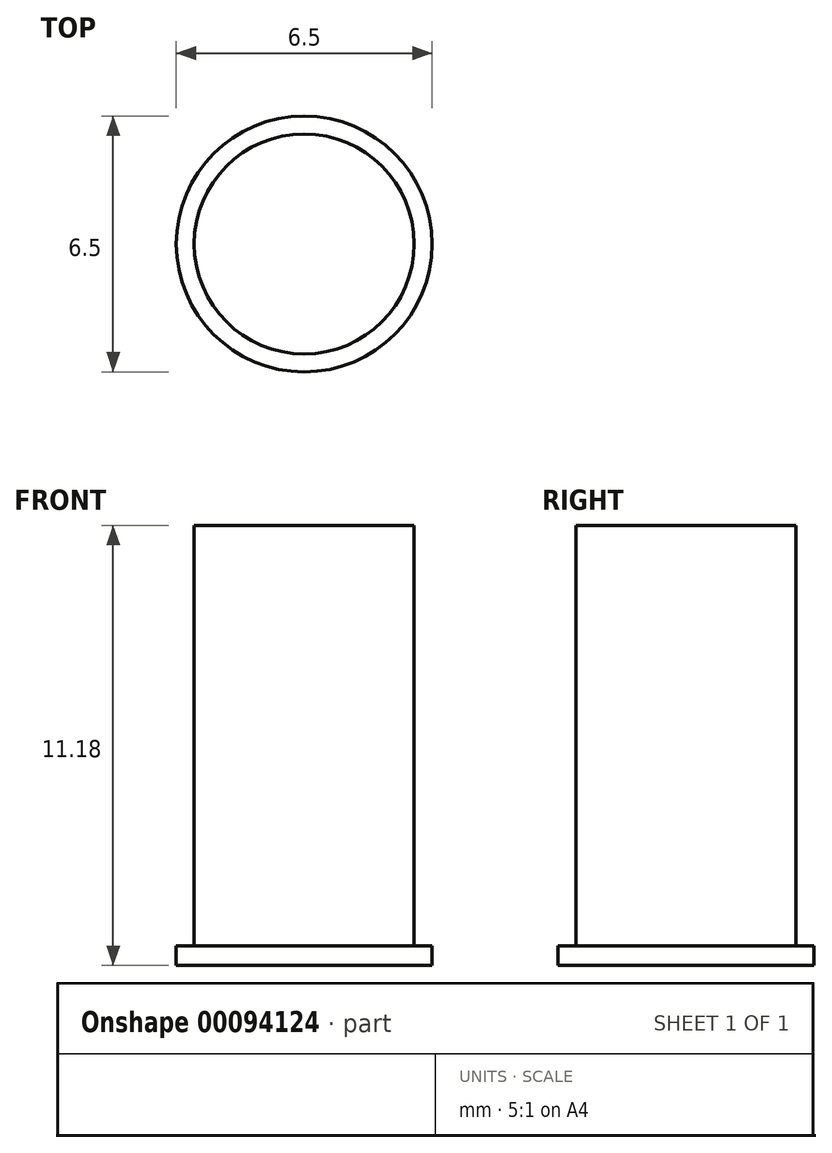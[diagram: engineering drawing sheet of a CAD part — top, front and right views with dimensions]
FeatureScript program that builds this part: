
annotation { "Feature Type Name" : "Feature", "Feature Type Description" : "" }
export const myFeature = defineFeature(function(context is Context, id is Id, definition is map)
    precondition{}
    {
        {
            var Q0;
            Q0=qCreatedBy(makeId("Top.planeOp"),FACE);
            var sketch = newSketch(context, id + "F0", { "sketchPlane" : qUnion([Q0])});
            skCircle(sketch, "E0", {"center": v(0, 0) * mm, "radius": 3.25 * mm});
            skCircle(sketch, "E1", {"center": v(0, 0) * mm, "radius": 2.8 * mm});
            skSolve(sketch);
        }
        {
            var Q0;
            Q0=makeQuery(id+"F0.imprint","IMPRINT",FACE,{"disambiguationData":[TD([[makeQuery(id+"F0.imprint","IMPRINT",EDGE,{"derivedFrom":sQuery(id+"F0.wireOp",EDGE,"E0")}),1.0]])]});
            var Q1;
            Q1=makeQuery(id+"F0.imprint","IMPRINT",FACE,{"disambiguationData":[TD([[makeQuery(id+"F0.imprint","IMPRINT",EDGE,{"derivedFrom":sQuery(id+"F0.wireOp",EDGE,"E1")}),1.0]])]});
            extrude(context, id + "F1", {"entities" : qUnion([Q0, Q1]), "depth" : 0.5 * mm});
        }
        {
            var Q0;
            Q0=makeQuery(id+"F0.imprint","IMPRINT",FACE,{"disambiguationData":[TD([[makeQuery(id+"F0.imprint","IMPRINT",EDGE,{"derivedFrom":sQuery(id+"F0.wireOp",EDGE,"E1")}),1.0]])]});
            extrude(context, id + "F2", {"entities" : qUnion([Q0]), "operationType" : NewBodyOperationType.ADD, "depth" : 11.18 * mm});
        }
    });
